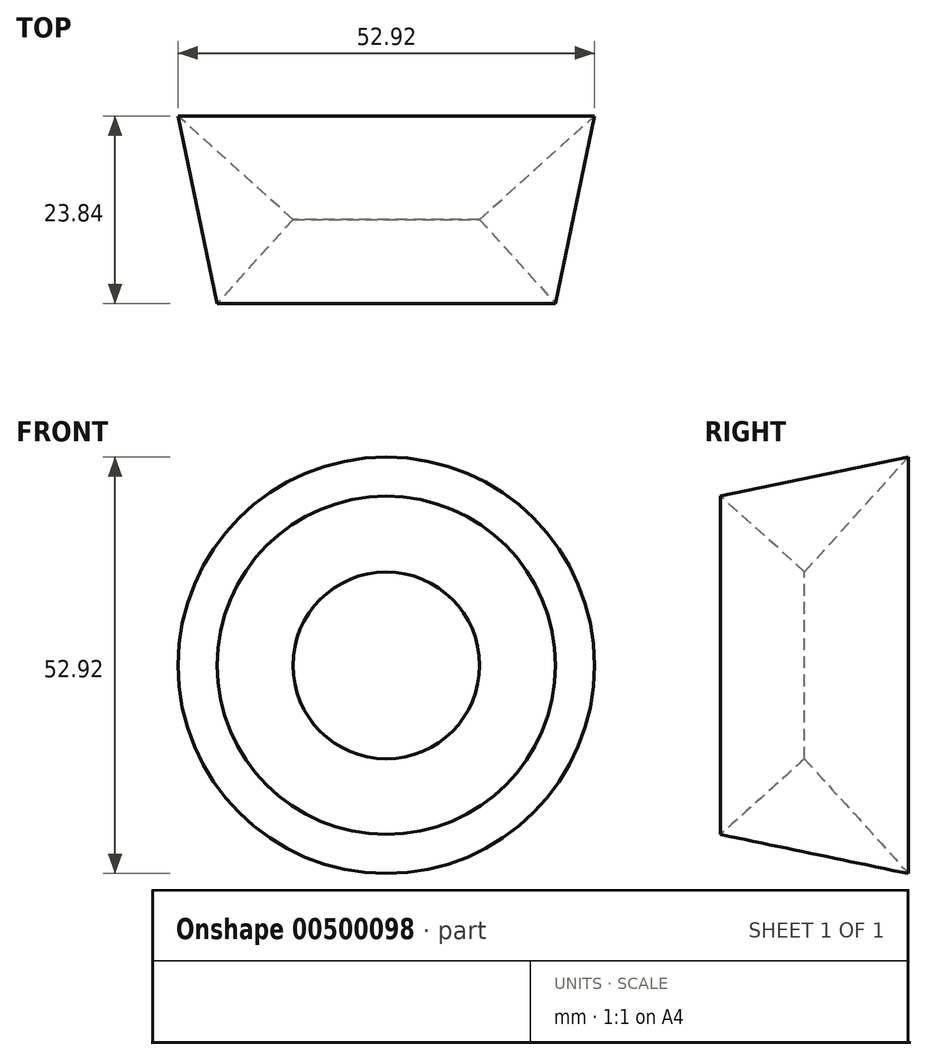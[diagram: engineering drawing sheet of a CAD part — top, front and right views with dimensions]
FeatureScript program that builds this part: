
annotation { "Feature Type Name" : "Feature", "Feature Type Description" : "" }
export const myFeature = defineFeature(function(context is Context, id is Id, definition is map)
    precondition{}
    {
        {
            var Q0;
            Q0=qCreatedBy(makeId("Top.planeOp"),FACE);
            var sketch = newSketch(context, id + "F0", { "sketchPlane" : qUnion([Q0])});
            skLineSegment(sketch, "E0", {"start": v(0, 0) * mm, "end": v(0, 23.84) * mm});
            skLineSegment(sketch, "E1", {"start": v(0, 23.84) * mm, "end": v(21.5, 0) * mm});
            skLineSegment(sketch, "E2", {"start": v(21.5, 0) * mm, "end": v(26.46, 23.84) * mm});
            skLineSegment(sketch, "E3", {"start": v(0, 0) * mm, "end": v(26.46, 23.84) * mm});
            skSolve(sketch);
        }
        {
            var Q0;
            Q0=qCreatedBy(makeId("Top.planeOp"),FACE);
            cPlane(context, id + "F1", {"entities" : qUnion([Q0]), "cplaneType" : CPlaneType.OFFSET, "offset" : 100 * mm, "width" : 150 * mm, "height" : 150 * mm});
        }
        {
            var Q0;
            {var subQ0=sQuery(id+"F0.wireOp",EDGE,"E2");Q0=makeQuery(id+"F0.imprint","IMPRINT",FACE,{"disambiguationData":[TD([[makeQuery(id+"F0.imprint","IMPRINT",EDGE,{"derivedFrom":subQ0}),1.0]])]});}
            var Q1;
            Q1=sQuery(id+"F0.wireOp",EDGE,"E0");
            revolve(context, id + "F2", {"entities" : qUnion([Q0]), "axis" : qUnion([Q1]), "revolveType" : RevolveType.FULL});
        }
    });
